# Revit family: Rundstahlbügel, Ø 21,3- 88,9, V4A
name_source: partatom
category: HLS-Bauteile
revit_build: Autodesk Revit 2017 (Build: 20190507_1515(x64)
units: mm (PartAtom-declared; Revit-internal decimal feet)

## family parameters
Arbeitsebenenbasiert = Ja
Beim Laden mit Abzugskörper schneiden = Nein
Bemaßung runder Anschluss = Durchmesser verwenden
Gemeinsam genutzt = Ja
Immer vertikal = Nein
Raumberechnungspunkt = Nein
Teiletyp = Normal

## types (8) — shared parameters
Fabrikat = MEFA
Firma = MEFA Befestigungs- und Montagesysteme GmbH
Kurztext1 = Rundstahlbügel V4A
Material = Edelstahl
Materialname = V4A
Oberflaeche = Edelstahl
Vorgabe-Ansicht = 1219 mm
max. Profilhöhe = 40 mm  [stored 0.131234 ft]
vpe = 1 St

## per-type parameters (varying)
| type | A | Achsabstand | Artikelnummer | B | EAN | Gewicht | Gewicht pro Bauteil | Gewinde | H | Höhe | Kurztext2 | L1 | Länge Gewinde | M | Nennweite DN Rohr | Rohraußendurchmesser | Rohraußendurchmesser Zoll | d2 |
| Rundstahlbügel, M 8, Ø 21,3, V4A | 30 mm  [stored 0.0984252 ft] | 30 mm | 0506022 | 65 mm  [stored 0.213255 ft] | 4250928414076 | 0.06 kg | 0.06 kg | M8 | 80 mm  [stored 0.262467 ft] | 80 mm | 21.3 mm M8 Gesamthöhe 80 mm | 4 mm  [stored 0.0131234 ft] | 65 mm  [stored 0.213255 ft] | 8 mm  [stored 0.0262467 ft] | 15 mm  [stored 0.0492126 ft] | 21 mm | 1/2 Zoll | 8 mm  [stored 0.0262467 ft] |
| Rundstahlbügel, M 8, Ø 25- 26,9, V4A | 35 mm  [stored 0.114829 ft] | 35 mm | 0506027 | 65 mm  [stored 0.213255 ft] | 4250928414083 | 0.06 kg | 0.06 kg | M8 | 80 mm  [stored 0.262467 ft] | 80 mm | 26.9 mm M8 Gesamthöhe 80 mm | 2 mm  [stored 0.00656168 ft] | 65 mm  [stored 0.213255 ft] | 8 mm  [stored 0.0262467 ft] | 20 mm  [stored 0.0656168 ft] | 27 mm | 3/4 Zoll | 8 mm  [stored 0.0262467 ft] |
| Rundstahlbügel, M 8, Ø 30- 33,7, V4A | 35 mm  [stored 0.114829 ft] | 42 mm | 0506034 | 65 mm  [stored 0.213255 ft] | 4250928414090 | 0.07 kg | 0.07 kg | M8 | 90 mm  [stored 0.295276 ft] | 90 mm | 33.7 mm M8 Gesamthöhe 90 mm | 12 mm  [stored 0.0393701 ft] | 65 mm  [stored 0.213255 ft] | 8 mm  [stored 0.0262467 ft] | 25 mm  [stored 0.082021 ft] | 34 mm | 1 Zoll | 8 mm  [stored 0.0262467 ft] |
| Rundstahlbügel, M 8, Ø 38- 42,4, V4A | 51 mm | 51 mm | 0506042 | 70 mm  [stored 0.229659 ft] | 4250928414106 | 0.08 kg | 0.08 kg | M8 | 100 mm  [stored 0.328084 ft] | 100 mm | 42.4 mm M8 Gesamthöhe 100 mm | 9 mm | 70 mm  [stored 0.229659 ft] | 8 mm  [stored 0.0262467 ft] | 32 mm  [stored 0.104987 ft] | 42 mm | 1 1/4 Zoll | 8 mm  [stored 0.0262467 ft] |
| Rundstahlbügel, M 8, Ø 44,5- 48,3, V4A | 57 mm  [stored 0.187008 ft] | 57 mm | 0506048 | 70 mm  [stored 0.229659 ft] | 4250928414113 | 0.08 kg | 0.08 kg | M8 | 105 mm  [stored 0.344488 ft] | 105 mm | 48.3 mm M8 Gesamthöhe 105 mm | 11 mm | 70 mm  [stored 0.229659 ft] | 8 mm  [stored 0.0262467 ft] | 40 mm  [stored 0.131234 ft] | 48 mm | 1 1/2 Zoll | 8 mm  [stored 0.0262467 ft] |
| Rundstahlbügel, M10, Ø 57- 60,3, V4A | 71 mm  [stored 0.23294 ft] | 71 mm | 0506060 | 70 mm  [stored 0.229659 ft] | 4250928414120 | 0.15 kg | 0.15 kg | M10 | 120 mm  [stored 0.393701 ft] | 120 mm | 60.3 mm M10 Gesamthöhe 120 mm | 20 mm  [stored 0.0656168 ft] | 70 mm  [stored 0.229659 ft] | 10 mm  [stored 0.0328084 ft] | 50 mm  [stored 0.164042 ft] | 60 mm | 2 Zoll | 10 mm  [stored 0.0328084 ft] |
| Rundstahlbügel, M10, Ø 76,1, V4A | 87 mm  [stored 0.285433 ft] | 87 mm | 0506076 | 70 mm  [stored 0.229659 ft] | 4250928414137 | 0.17 kg | 0.17 kg | M10 | 135 mm  [stored 0.442913 ft] | 135 mm | 76.1 mm M10 Gesamthöhe 135 mm | 27 mm | 70 mm  [stored 0.229659 ft] | 10 mm  [stored 0.0328084 ft] | 65 mm  [stored 0.213255 ft] | 76 mm | 2 1/2 Zoll | 10 mm  [stored 0.0328084 ft] |
| Rundstahlbügel, M10, Ø 88,9, V4A | 100 mm  [stored 0.328084 ft] | 100 mm | 0506089 | 70 mm  [stored 0.229659 ft] | 4250928414144 | 0.19 kg | 0.19 kg | M10 | 150 mm | 150 mm | 88.9 mm M10 Gesamthöhe 150 mm | 35 mm  [stored 0.114829 ft] | 70 mm  [stored 0.229659 ft] | 10 mm  [stored 0.0328084 ft] | 80 mm  [stored 0.262467 ft] | 89 mm | 3 Zoll | 10 mm  [stored 0.0328084 ft] |

note: [stored X ft] marks values corroborated as IEEE doubles in the binary element streams (Revit-internal decimal feet)
